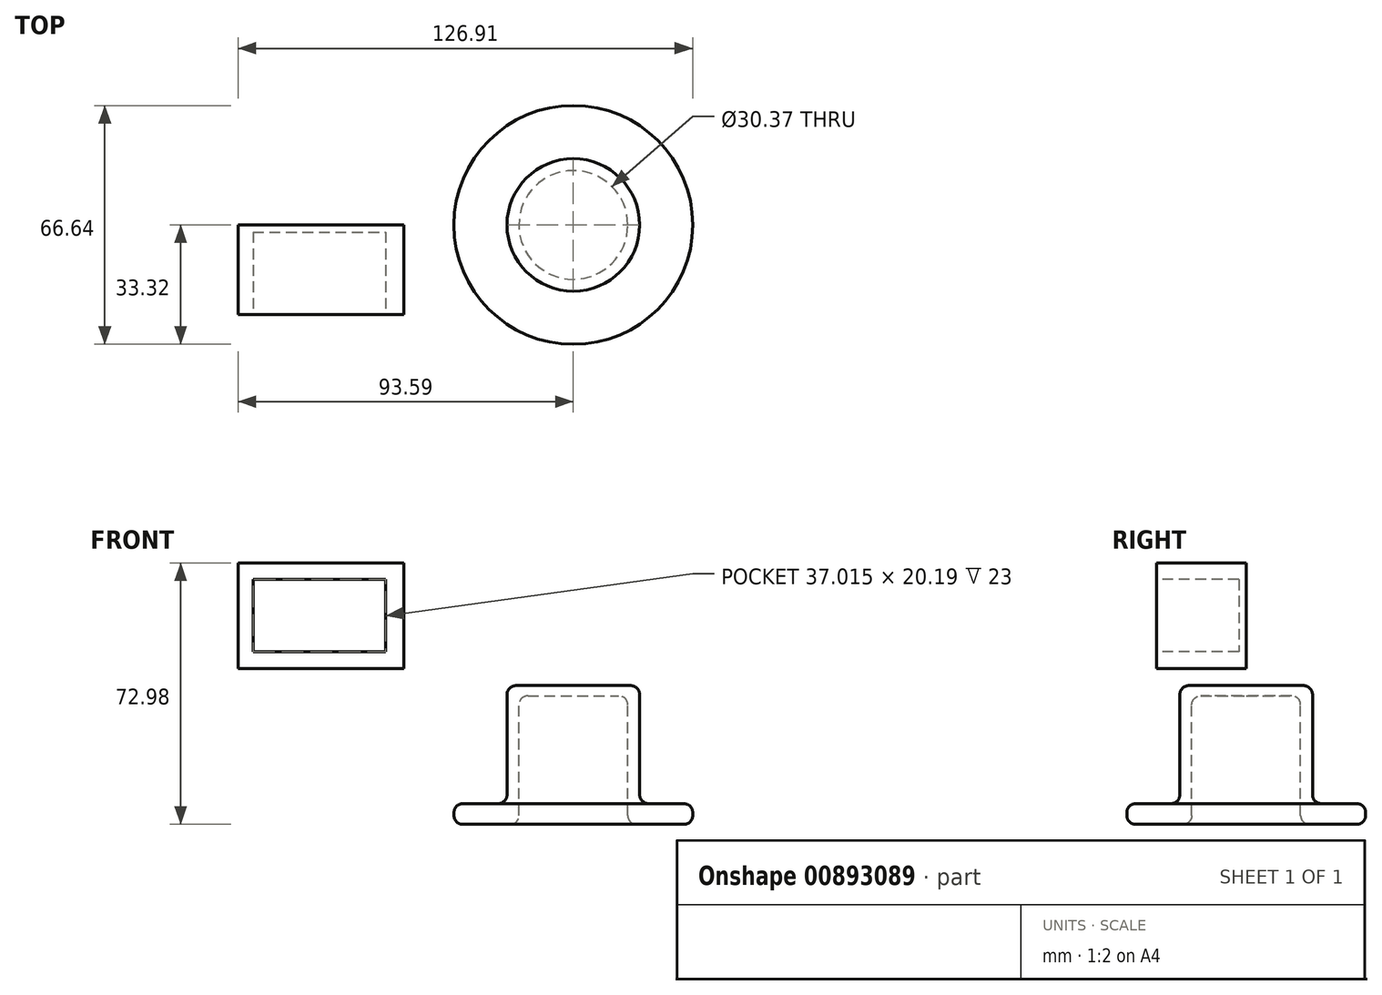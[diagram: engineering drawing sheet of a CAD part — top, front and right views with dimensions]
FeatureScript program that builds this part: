
annotation { "Feature Type Name" : "Feature", "Feature Type Description" : "" }
export const myFeature = defineFeature(function(context is Context, id is Id, definition is map)
    precondition{}
    {
        {
            var Q0;
            Q0=qCreatedBy(makeId("Front.planeOp"),FACE);
            var sketch = newSketch(context, id + "F0", { "sketchPlane" : qUnion([Q0])});
            skLineSegment(sketch, "E0", {"start": v(0, 38.74) * mm, "end": v(18.5, 38.74) * mm});
            skLineSegment(sketch, "E1", {"start": v(18.5, 38.74) * mm, "end": v(18.5, 5.78) * mm});
            skLineSegment(sketch, "E2", {"start": v(18.5, 5.78) * mm, "end": v(33.32, 5.78) * mm});
            skLineSegment(sketch, "E3", {"start": v(33.32, 5.78) * mm, "end": v(33.32, 0) * mm});
            skLineSegment(sketch, "E4", {"start": v(33.32, 0) * mm, "end": v(15.18, 0) * mm});
            skLineSegment(sketch, "E5", {"start": v(15.18, 0) * mm, "end": v(15.18, 35.86) * mm});
            skLineSegment(sketch, "E6", {"start": v(15.18, 35.86) * mm, "end": v(0, 35.86) * mm});
            skLineSegment(sketch, "E7", {"start": v(0, 38.74) * mm, "end": v(0, 35.86) * mm});
            skSolve(sketch);
        }
        {
            var Q0;
            Q0=makeQuery(id+"F0.imprint","IMPRINT",FACE,{"disambiguationData":[TD([[makeQuery(id+"F0.imprint","IMPRINT",EDGE,{"derivedFrom":sQuery(id+"F0.wireOp",EDGE,"E0")}),-1.0]])]});
            var Q1;
            Q1=sQuery(id+"F0.wireOp",EDGE,"E7");
            revolve(context, id + "F1", {"surfaceOperationType" : NewSurfaceOperationType.NEW, "entities" : qUnion([Q0]), "axis" : qUnion([Q1]), "revolveType" : RevolveType.FULL});
        }
        {
            var Q0;
            Q0=makeQuery(id+"F1.opRevolve","SWEPT_EDGE",EDGE,{"disambiguationData":[OSD([sQuery(id+"F0.wireOp",EDGE,"E5"),sQuery(id+"F0.wireOp",EDGE,"E6")])]});
            var Q1;
            Q1=makeQuery(id+"F1.opRevolve","SWEPT_EDGE",EDGE,{"disambiguationData":[OSD([sQuery(id+"F0.wireOp",EDGE,"E4"),sQuery(id+"F0.wireOp",EDGE,"E5")])]});
            var Q2;
            Q2=makeQuery(id+"F1.opRevolve","SWEPT_EDGE",EDGE,{"disambiguationData":[OSD([sQuery(id+"F0.wireOp",EDGE,"E2"),sQuery(id+"F0.wireOp",EDGE,"E3")])]});
            var Q3;
            Q3=makeQuery(id+"F1.opRevolve","SWEPT_EDGE",EDGE,{"disambiguationData":[OSD([sQuery(id+"F0.wireOp",EDGE,"E3"),sQuery(id+"F0.wireOp",EDGE,"E4")])]});
            var Q4;
            Q4=makeQuery(id+"F1.opRevolve","SWEPT_EDGE",EDGE,{"disambiguationData":[OSD([sQuery(id+"F0.wireOp",EDGE,"E1"),sQuery(id+"F0.wireOp",EDGE,"E2")])]});
            var Q5;
            Q5=makeQuery(id+"F1.opRevolve","SWEPT_EDGE",EDGE,{"disambiguationData":[OSD([sQuery(id+"F0.wireOp",EDGE,"E0"),sQuery(id+"F0.wireOp",EDGE,"E1")])]});
            fillet(context, id + "F2", {"entities" : qUnion([Q0, Q1, Q2, Q3, Q4, Q5]), "radius" : 2.5 * mm, "tangentPropagation" : true, "allowEdgeOverflow" : false});
        }
        {
            var Q0;
            Q0=qCreatedBy(makeId("Front.planeOp"),FACE);
            var sketch = newSketch(context, id + "F3", { "sketchPlane" : qUnion([Q0])});
            skLineSegment(sketch, "E8.bottom", {"start": v(-93.59, 72.98) * mm, "end": v(-47.32, 72.98) * mm});
            skLineSegment(sketch, "E8.top", {"start": v(-93.59, 43.53) * mm, "end": v(-47.32, 43.53) * mm});
            skLineSegment(sketch, "E8.left", {"start": v(-93.59, 72.98) * mm, "end": v(-93.59, 43.53) * mm});
            skLineSegment(sketch, "E8.right", {"start": v(-47.32, 72.98) * mm, "end": v(-47.32, 43.53) * mm});
            skSolve(sketch);
        }
        {
            var Q0;
            Q0=makeQuery(id+"F3.imprint","IMPRINT",FACE,{"disambiguationData":[TD([[makeQuery(id+"F3.imprint","IMPRINT",EDGE,{"derivedFrom":sQuery(id+"F3.wireOp",EDGE,"E8.bottom")}),-1.0]])]});
            extrude(context, id + "F4", {"entities" : qUnion([Q0]), "depth" : 25 * mm, "offsetDistance" : 25 * mm});
        }
        {
            var Q0;
            Q0=makeQuery(id+"F4.opExtrude","CAP_FACE",FACE,{"disambiguationData":[OSD([sQuery(id+"F3.wireOp",EDGE,"E8.bottom"),sQuery(id+"F3.wireOp",EDGE,"E8.top"),sQuery(id+"F3.wireOp",EDGE,"E8.left"),sQuery(id+"F3.wireOp",EDGE,"E8.right")])],"isStart":false});
            var sketch = newSketch(context, id + "F5", { "sketchPlane" : qUnion([Q0])});
            skLineSegment(sketch, "E9.bottom", {"start": v(-89.38, 68.35) * mm, "end": v(-52.37, 68.35) * mm});
            skLineSegment(sketch, "E9.top", {"start": v(-89.38, 48.16) * mm, "end": v(-52.37, 48.16) * mm});
            skLineSegment(sketch, "E9.left", {"start": v(-89.38, 68.35) * mm, "end": v(-89.38, 48.16) * mm});
            skLineSegment(sketch, "E9.right", {"start": v(-52.37, 68.35) * mm, "end": v(-52.37, 48.16) * mm});
            skSolve(sketch);
        }
        {
            var Q0;
            Q0=makeQuery(id+"F5.imprint","IMPRINT",FACE,{"disambiguationData":[TD([[makeQuery(id+"F5.imprint","IMPRINT",EDGE,{"derivedFrom":sQuery(id+"F5.wireOp",EDGE,"E9.bottom")}),-1.0]])]});
            extrude(context, id + "F6", {"entities" : qUnion([Q0]), "operationType" : NewBodyOperationType.REMOVE, "oppositeDirection" : true, "depth" : 23 * mm, "offsetDistance" : 25 * mm});
        }
    });
